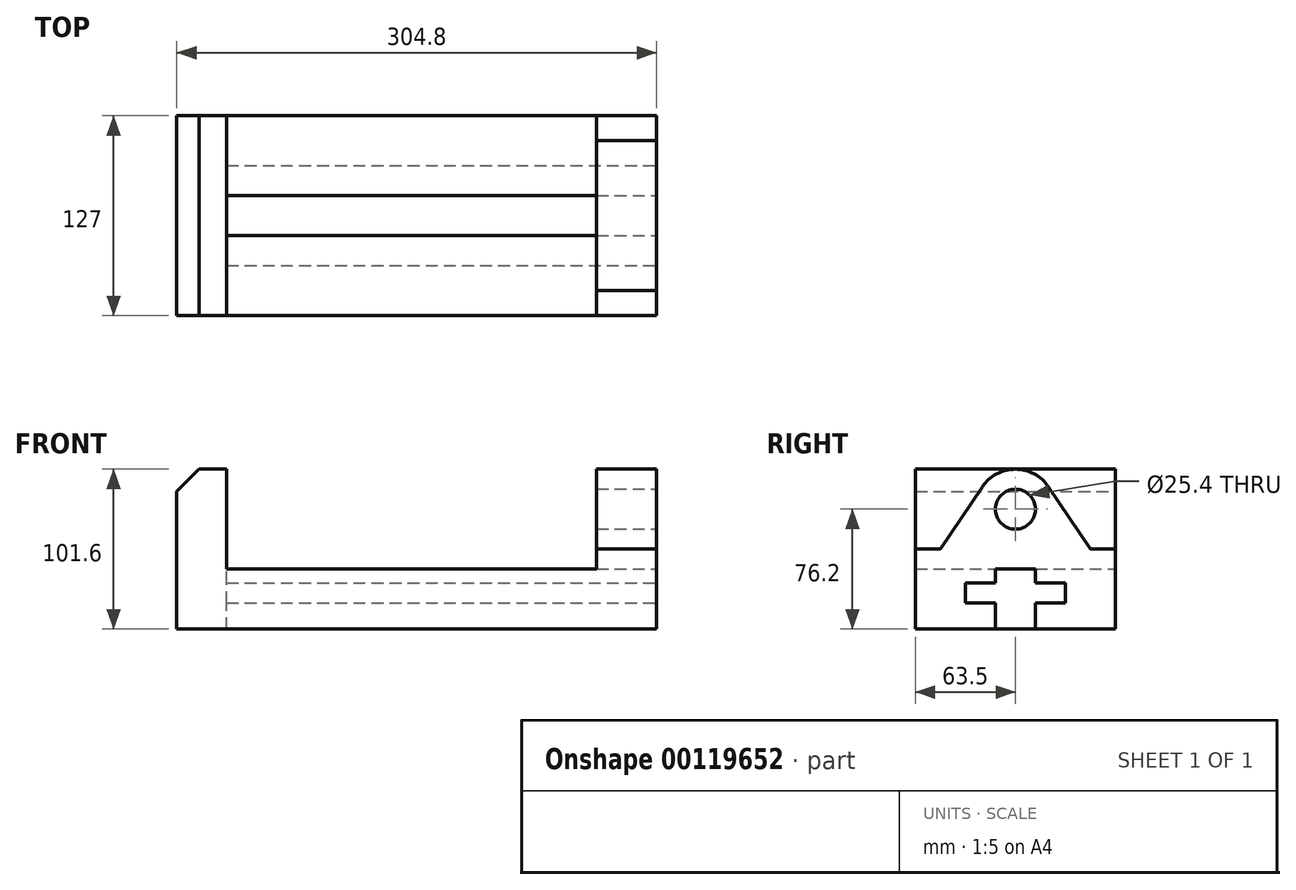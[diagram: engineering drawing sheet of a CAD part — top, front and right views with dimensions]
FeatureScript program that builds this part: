
annotation { "Feature Type Name" : "Feature", "Feature Type Description" : "" }
export const myFeature = defineFeature(function(context is Context, id is Id, definition is map)
    precondition{}
    {
        {
            var Q0;
            Q0=qCreatedBy(makeId("Front.planeOp"),FACE);
            var sketch = newSketch(context, id + "F0", { "sketchPlane" : qUnion([Q0])});
            skLineSegment(sketch, "E0", {"start": v(0, 0) * mm, "end": v(0, 50.8) * mm});
            skLineSegment(sketch, "E1", {"start": v(0, 50.8) * mm, "end": v(-38.1, 50.8) * mm});
            skLineSegment(sketch, "E2", {"start": v(-273.05, 101.6) * mm, "end": v(-304.8, 101.6) * mm});
            skLineSegment(sketch, "E3", {"start": v(-304.8, 101.6) * mm, "end": v(-304.8, 0) * mm});
            skLineSegment(sketch, "E4", {"start": v(-304.8, 0) * mm, "end": v(0, 0) * mm});
            skLineSegment(sketch, "E5", {"start": v(-273.05, 101.6) * mm, "end": v(-273.05, 38.1) * mm});
            skLineSegment(sketch, "E6", {"start": v(-273.05, 38.1) * mm, "end": v(-38.1, 38.1) * mm});
            skLineSegment(sketch, "E7", {"start": v(-38.1, 38.1) * mm, "end": v(-38.1, 50.8) * mm});
            skSolve(sketch);
        }
        {
            var Q0;
            Q0=makeQuery(id+"F0.imprint","IMPRINT",FACE,{"disambiguationData":[TD([[makeQuery(id+"F0.imprint","IMPRINT",EDGE,{"derivedFrom":sQuery(id+"F0.wireOp",EDGE,"E0")}),1.0]])]});
            extrude(context, id + "F1", {"entities" : qUnion([Q0]), "endBound" : BoundingType.SYMMETRIC, "depth" : 127 * mm});
        }
        {
            var Q0;
            Q0=makeQuery(id+"F1.opExtrude","SWEPT_EDGE",EDGE,{"disambiguationData":[OSD([sQuery(id+"F0.wireOp",EDGE,"E2"),sQuery(id+"F0.wireOp",EDGE,"E3")])]});
            chamfer(context, id + "F2", {"entities" : qUnion([Q0]), "width" : 0.75 * 19.05 * mm, "tangentPropagation" : true});
        }
        {
            var Q0;
            Q0=qCreatedBy(makeId("Right.planeOp"),FACE);
            var sketch = newSketch(context, id + "F3", { "sketchPlane" : qUnion([Q0])});
            skLineSegment(sketch, "E8", {"start": v(-47.62, 50.8) * mm, "end": v(-21.1, 90.35) * mm});
            skLineSegment(sketch, "E9", {"start": v(47.62, 50.8) * mm, "end": v(21.1, 90.35) * mm});
            skLineSegment(sketch, "E10", {"start": v(-47.62, 50.8) * mm, "end": v(47.62, 50.8) * mm});
            skArc(sketch, "E11", {"start": v(-21.1, 90.35) * mm, "mid": v(0, 101.6) * mm, "end": v(21.1, 90.35) * mm});
            skCircle(sketch, "E12", {"center": v(0, 76.2) * mm, "radius": 12.7 * mm});
            skLineSegment(sketch, "E13", {"start": v(-12.7, 0) * mm, "end": v(12.7, 0) * mm});
            skLineSegment(sketch, "E14", {"start": v(-12.7, 38.1) * mm, "end": v(12.7, 38.1) * mm});
            skLineSegment(sketch, "E15", {"start": v(12.7, 38.1) * mm, "end": v(12.7, 29.21) * mm});
            skLineSegment(sketch, "E16", {"start": v(12.7, 29.21) * mm, "end": v(31.75, 29.21) * mm});
            skLineSegment(sketch, "E17", {"start": v(31.75, 29.21) * mm, "end": v(31.75, 16.51) * mm});
            skLineSegment(sketch, "E18", {"start": v(31.75, 16.51) * mm, "end": v(12.7, 16.51) * mm});
            skLineSegment(sketch, "E19", {"start": v(12.7, 16.51) * mm, "end": v(12.7, 0) * mm});
            skLineSegment(sketch, "E20", {"start": v(-12.7, 0) * mm, "end": v(-12.7, 16.51) * mm});
            skLineSegment(sketch, "E21", {"start": v(-12.7, 16.51) * mm, "end": v(-31.75, 16.51) * mm});
            skLineSegment(sketch, "E22", {"start": v(-31.75, 16.51) * mm, "end": v(-31.75, 29.21) * mm});
            skLineSegment(sketch, "E23", {"start": v(-31.75, 29.21) * mm, "end": v(-12.7, 29.21) * mm});
            skLineSegment(sketch, "E24", {"start": v(-12.7, 29.21) * mm, "end": v(-12.7, 38.1) * mm});
            skSolve(sketch);
        }
        {
            var Q0;
            Q0=makeQuery(id+"F3.imprint","IMPRINT",FACE,{"disambiguationData":[TD([[makeQuery(id+"F3.imprint","IMPRINT",EDGE,{"derivedFrom":sQuery(id+"F3.wireOp",EDGE,"E8")}),-1.0]])]});
            extrude(context, id + "F4", {"entities" : qUnion([Q0]), "operationType" : NewBodyOperationType.ADD, "oppositeDirection" : true, "depth" : 38.1 * mm});
        }
        {
            var Q0;
            Q0=makeQuery(id+"F3.imprint","IMPRINT",FACE,{"disambiguationData":[TD([[makeQuery(id+"F3.imprint","IMPRINT",EDGE,{"derivedFrom":sQuery(id+"F3.wireOp",EDGE,"E13")}),1.0]])]});
            extrude(context, id + "F5", {"entities" : qUnion([Q0]), "operationType" : NewBodyOperationType.REMOVE, "oppositeDirection" : true, "depth" : 273.05 * mm});
        }
    });
